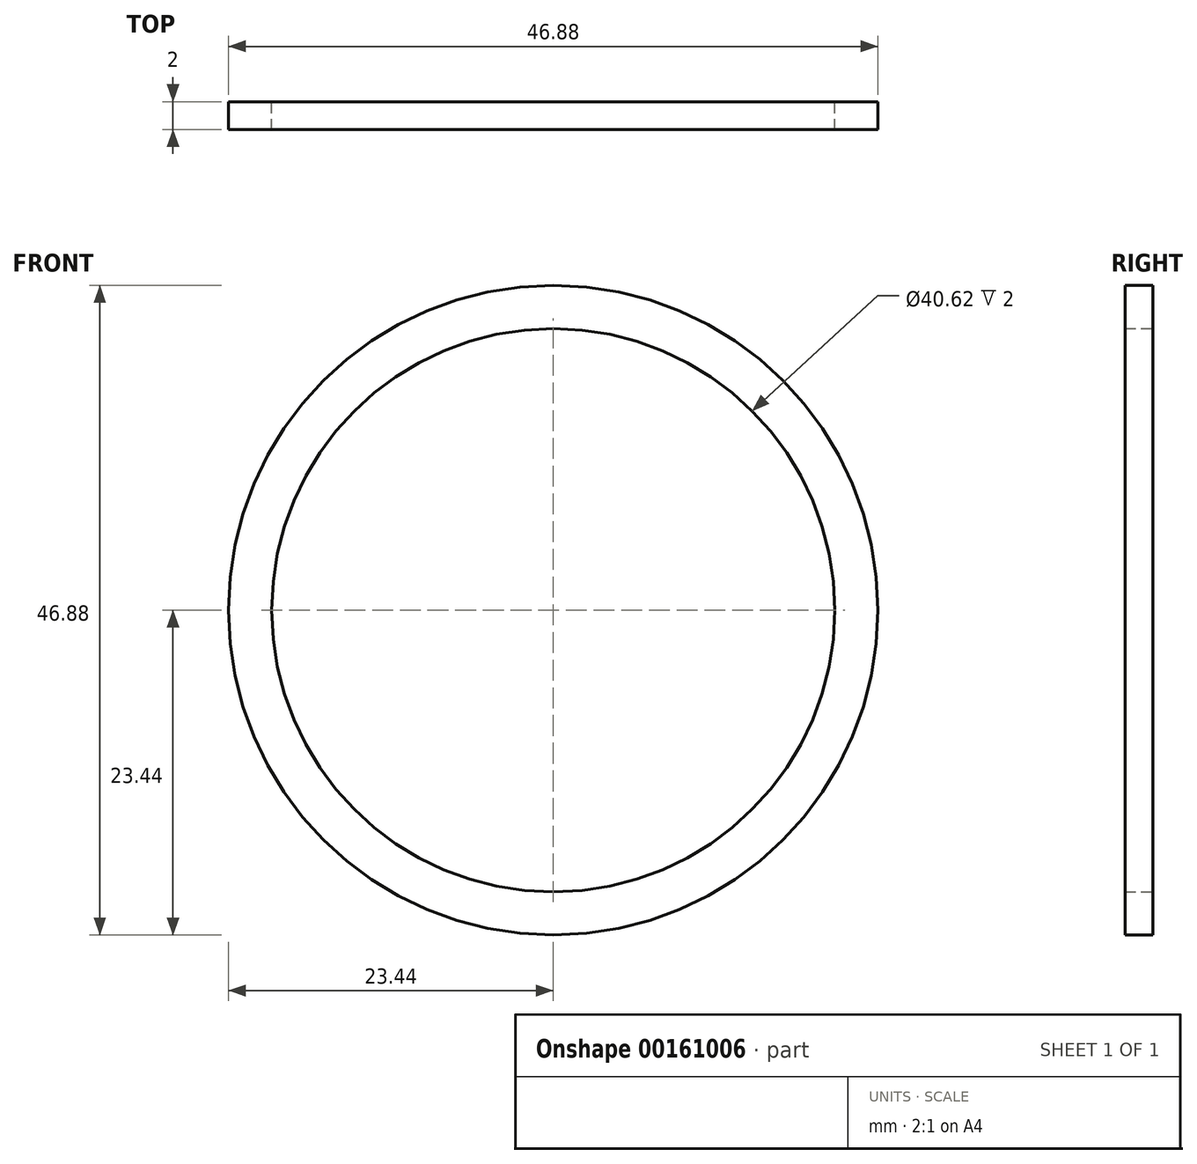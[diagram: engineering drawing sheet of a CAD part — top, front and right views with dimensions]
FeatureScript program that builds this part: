
annotation { "Feature Type Name" : "Feature", "Feature Type Description" : "" }
export const myFeature = defineFeature(function(context is Context, id is Id, definition is map)
    precondition{}
    {
        {
            var Q0;
            Q0=qCreatedBy(makeId("Front.planeOp"),FACE);
            var sketch = newSketch(context, id + "F0", { "sketchPlane" : qUnion([Q0])});
            skCircle(sketch, "E0", {"center": v(0, 0) * mm, "radius": 23.44 * mm});
            skCircle(sketch, "E1", {"center": v(0, 0) * mm, "radius": 20.31 * mm});
            skCircle(sketch, "E2", {"center": v(0, 0) * mm, "radius": 3.5 * mm});
            skSolve(sketch);
        }
        {
            var Q0;
            Q0=makeQuery(id+"F0.imprint","IMPRINT",FACE,{"disambiguationData":[TD([[makeQuery(id+"F0.imprint","IMPRINT",EDGE,{"derivedFrom":sQuery(id+"F0.wireOp",EDGE,"E0")}),1.0]])]});
            extrude(context, id + "F1", {"entities" : qUnion([Q0]), "depth" : 2 * mm});
        }
    });
